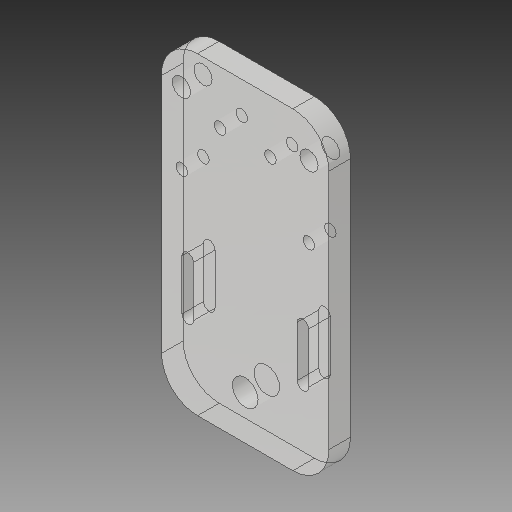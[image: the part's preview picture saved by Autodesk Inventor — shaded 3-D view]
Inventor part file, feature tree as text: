
AUTODESK INVENTOR PART (.ipt)
format: ipt  version: 2018 (Build 220112000, 112)  size: 196,096 bytes
history: native  units: mm
features: other x3, sketch x2
ambient origin geometry x8: Origin, YZ Plane, XZ Plane, XY Plane, X Axis, Y Axis, Z Axis, Center Point
bodies: Solid1 (feature_tree)
feature tree (5):
  other  "Hotend Front Plate revised.ipt"
  other  "Solid1::Hotend Front Plate revised.ipt"
  other  "TaggingFeature1"
  sketch  "Sketch1"  dims[d0=10.0mm]
  sketch  "Sketch2"
